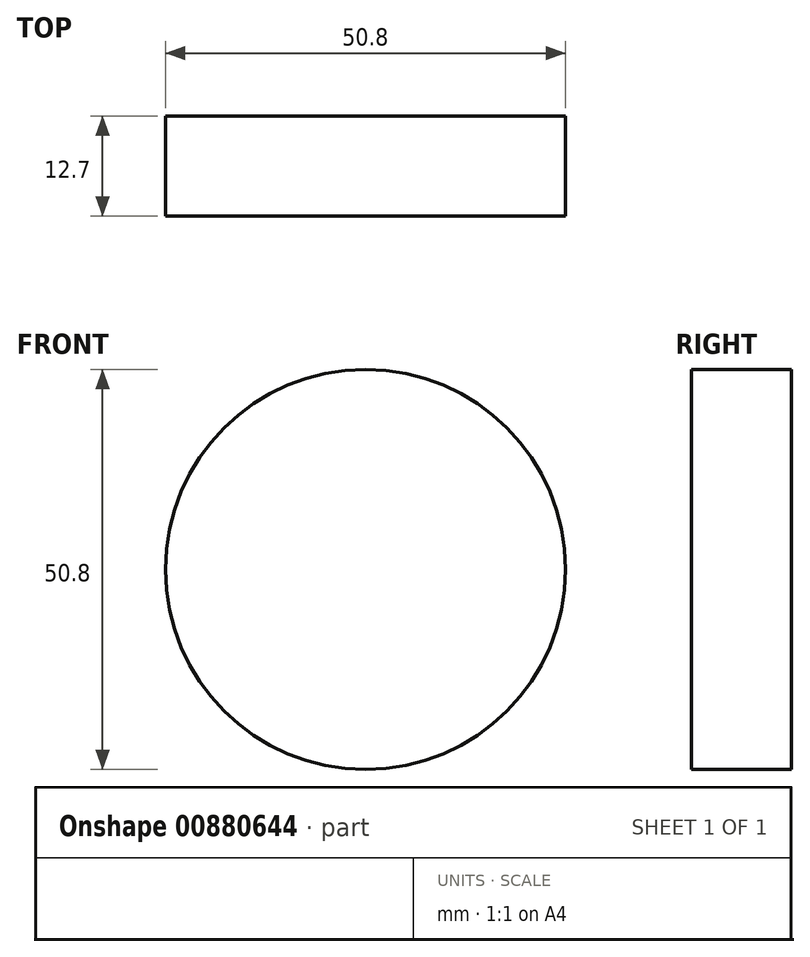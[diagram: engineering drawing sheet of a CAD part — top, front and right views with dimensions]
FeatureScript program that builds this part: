
annotation { "Feature Type Name" : "Feature", "Feature Type Description" : "" }
export const myFeature = defineFeature(function(context is Context, id is Id, definition is map)
    precondition{}
    {
        {
            var Q0;
            Q0=qCreatedBy(makeId("Front.planeOp"),FACE);
            var sketch = newSketch(context, id + "F0", { "sketchPlane" : qUnion([Q0])});
            skCircle(sketch, "E0", {"center": v(0, 0) * mm, "radius": 25.4 * mm});
            skSolve(sketch);
        }
        {
            var Q0;
            Q0 = qSketchRegion(id + "F0", true);
            extrude(context, id + "F1", {"entities" : qUnion([Q0]), "endBound" : BoundingType.SYMMETRIC, "depth" : 12.7 * mm, "offsetDistance" : 25.4 * mm});
        }
    });
